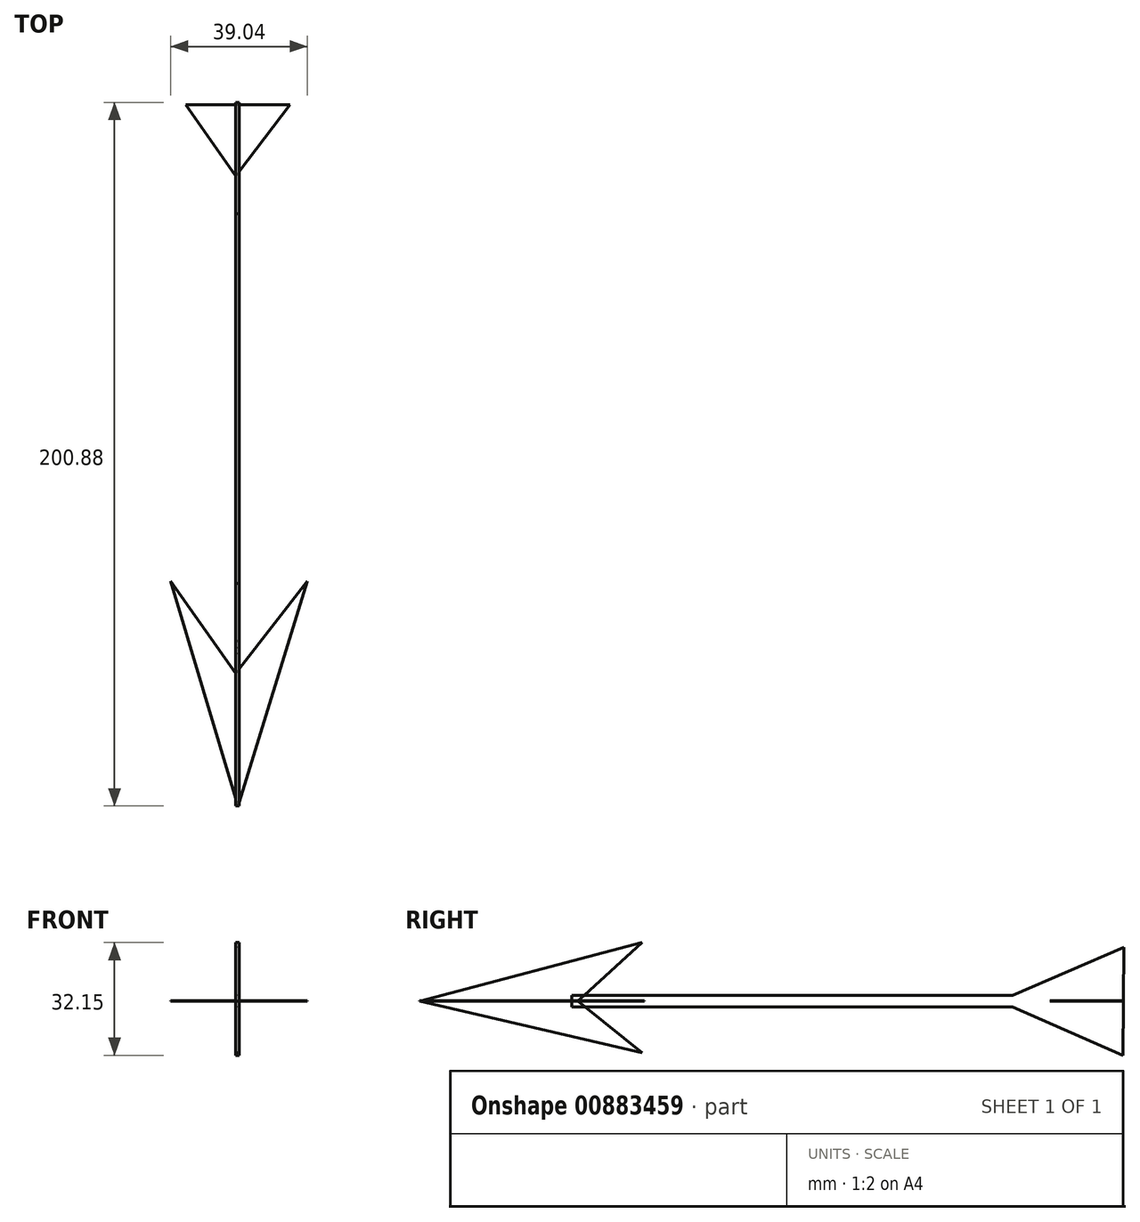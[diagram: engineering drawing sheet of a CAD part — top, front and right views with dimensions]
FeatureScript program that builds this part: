
annotation { "Feature Type Name" : "Feature", "Feature Type Description" : "" }
export const myFeature = defineFeature(function(context is Context, id is Id, definition is map)
    precondition{}
    {
        {
            var Q0;
            Q0=qCreatedBy(makeId("Right.planeOp"),FACE);
            var sketch = newSketch(context, id + "F0", { "sketchPlane" : qUnion([Q0])});
            skLineSegment(sketch, "E0.bottom", {"start": v(62.83, 1.64) * mm, "end": v(-62.83, 1.64) * mm});
            skLineSegment(sketch, "E0.top", {"start": v(62.83, -1.64) * mm, "end": v(-62.83, -1.64) * mm});
            skLineSegment(sketch, "E0.left", {"start": v(62.83, 1.64) * mm, "end": v(62.83, -1.64) * mm});
            skLineSegment(sketch, "E0.right", {"start": v(-62.83, 1.64) * mm, "end": v(-62.83, -1.64) * mm});
            skPoint(sketch, "E0.middle", {"position": v(0, 0) * mm});
            skLineSegment(sketch, "E1", {"start": v(62.83, 1.64) * mm, "end": v(94.62, 15.4) * mm});
            skLineSegment(sketch, "E2", {"start": v(94.62, 15.4) * mm, "end": v(94.4, -15.42) * mm});
            skLineSegment(sketch, "E3", {"start": v(94.4, -15.42) * mm, "end": v(62.83, -1.64) * mm});
            skLineSegment(sketch, "E4", {"start": v(0, 0) * mm, "end": v(-106.2, 0) * mm});
            skLineSegment(sketch, "E5", {"start": v(-106.2, 0) * mm, "end": v(-42.76, 16.73) * mm});
            skLineSegment(sketch, "E6", {"start": v(-42.76, 16.73) * mm, "end": v(-61.14, 0) * mm});
            skLineSegment(sketch, "E7", {"start": v(-61.14, 0) * mm, "end": v(-42.76, -14.77) * mm});
            skLineSegment(sketch, "E8", {"start": v(-42.76, -14.77) * mm, "end": v(-106.2, 0) * mm});
            skSolve(sketch);
        }
        {
            var Q0;
            {var subQ0=sQuery(id+"F0.wireOp",EDGE,"E0.left");Q0=makeQuery(id+"F0.imprint","IMPRINT",FACE,{"disambiguationData":[TD([[makeQuery(id+"F0.imprint","IMPRINT",EDGE,{"derivedFrom":subQ0}),-1.0]])]});}
            var Q1;
            {var subQ10=sQuery(id+"F0.wireOp",EDGE,"xE3pmvrO-ZM8g-4Rqy-bDu5-RwcSwtl96joR");Q1=makeQuery(id+"F0.imprint","IMPRINT",FACE,{"disambiguationData":[TD([[makeQuery(id+"F0.imprint","IMPRINT",EDGE,{"derivedFrom":subQ10}),1.0]])]});}
            var Q2;
            Q2=makeQuery(id+"F0.imprint","IMPRINT",FACE,{"disambiguationData":[TD([[makeQuery(id+"F0.imprint","IMPRINT",EDGE,{"derivedFrom":sQuery(id+"F0.wireOp",EDGE,"E0.left")}),1.0]])]});
            var Q3;
            {var subQ0=sQuery(id+"F0.wireOp",EDGE,"E5");Q3=makeQuery(id+"F0.imprint","IMPRINT",FACE,{"disambiguationData":[TD([[makeQuery(id+"F0.imprint","IMPRINT",EDGE,{"derivedFrom":subQ0}),-1.0]])]});}
            var Q4;
            {var subQ0=sQuery(id+"F0.wireOp",EDGE,"E8");Q4=makeQuery(id+"F0.imprint","IMPRINT",FACE,{"disambiguationData":[TD([[makeQuery(id+"F0.imprint","IMPRINT",EDGE,{"derivedFrom":subQ0}),-1.0]])]});}
            extrude(context, id + "F1", {"entities" : qUnion([Q0, Q1, Q2, Q3, Q4]), "depth" : 1 * mm, "offsetDistance" : 25 * mm});
        }
        {
            var Q0;
            Q0=qCreatedBy(makeId("Top.planeOp"),FACE);
            var sketch = newSketch(context, id + "F2", { "sketchPlane" : qUnion([Q0])});
            skLineSegment(sketch, "E9", {"start": v(0, 73.56) * mm, "end": v(-14.31, 93.92) * mm});
            skLineSegment(sketch, "E10", {"start": v(-14.31, 93.92) * mm, "end": v(15.5, 93.92) * mm});
            skLineSegment(sketch, "E11", {"start": v(15.5, 93.92) * mm, "end": v(0, 73.56) * mm});
            skLineSegment(sketch, "E12", {"start": v(0, -68.33) * mm, "end": v(-18.6, -42.12) * mm});
            skLineSegment(sketch, "E13", {"start": v(20.45, -42.12) * mm, "end": v(0, -68.33) * mm});
            skLineSegment(sketch, "E14", {"start": v(0.67, -106.26) * mm, "end": v(20.45, -42.12) * mm});
            skLineSegment(sketch, "E15", {"start": v(0.67, -106.26) * mm, "end": v(-18.6, -42.12) * mm});
            skSolve(sketch);
        }
        {
            var Q0;
            Q0=makeQuery(id+"F2.imprint","IMPRINT",FACE,{"disambiguationData":[TD([[makeQuery(id+"F2.imprint","IMPRINT",EDGE,{"derivedFrom":sQuery(id+"F2.wireOp",EDGE,"E12")}),1.0]])]});
            var Q1;
            Q1=makeQuery(id+"F2.imprint","IMPRINT",FACE,{"disambiguationData":[TD([[makeQuery(id+"F2.imprint","IMPRINT",EDGE,{"derivedFrom":sQuery(id+"F2.wireOp",EDGE,"E9")}),-1.0]])]});
            extrude(context, id + "F3", {"entities" : qUnion([Q0, Q1]), "depth" : 0.1 * mm, "offsetDistance" : 25 * mm});
        }
    });
